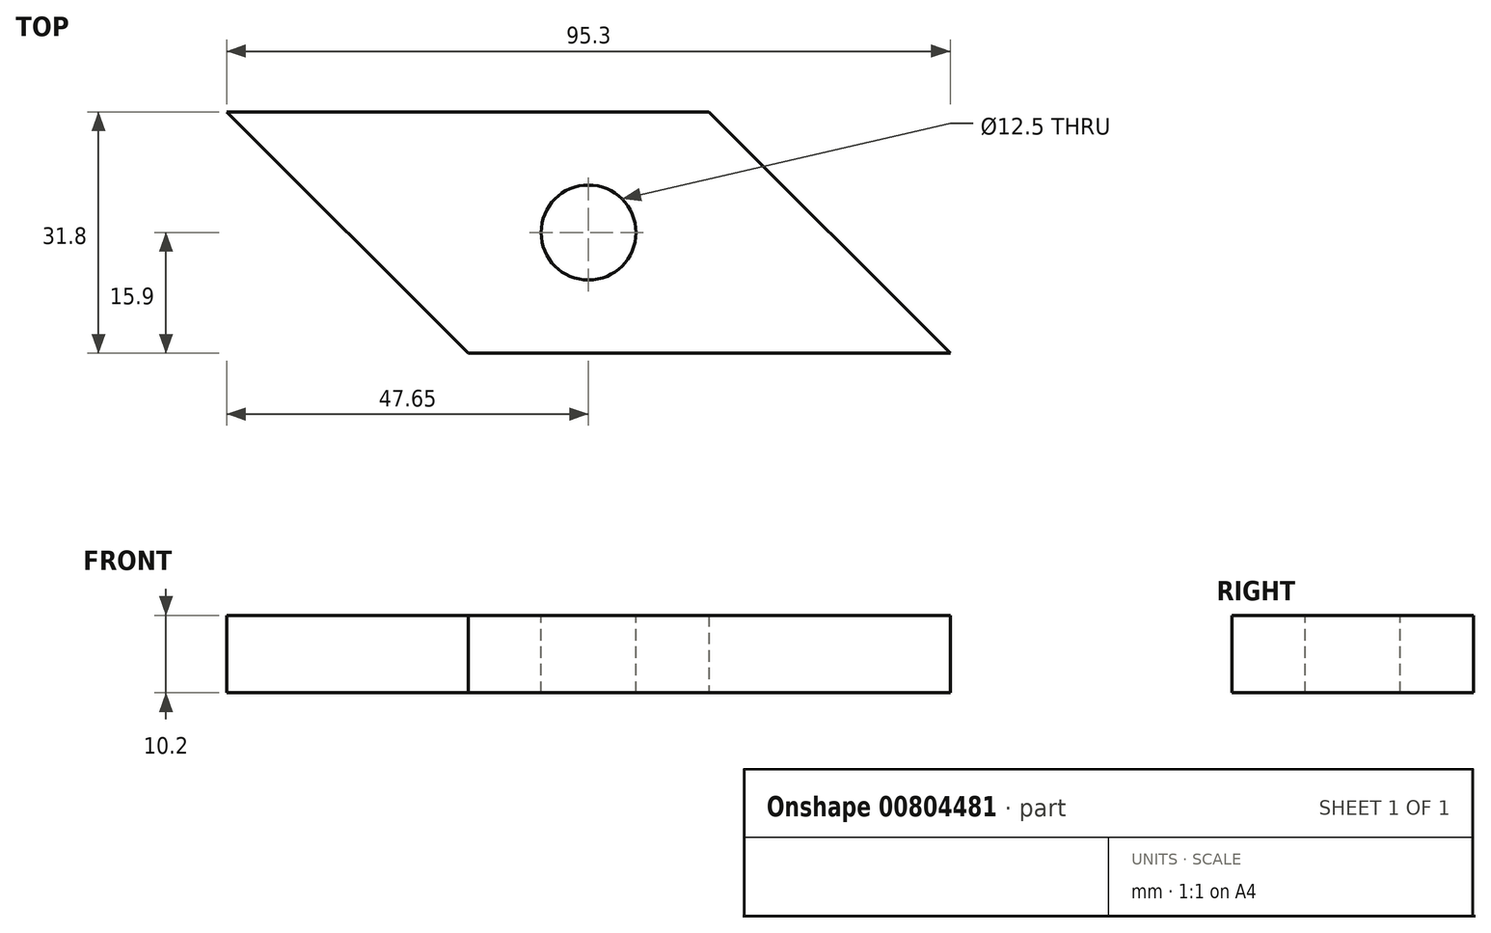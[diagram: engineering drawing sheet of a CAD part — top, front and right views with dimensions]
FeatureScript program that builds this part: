
annotation { "Feature Type Name" : "Feature", "Feature Type Description" : "" }
export const myFeature = defineFeature(function(context is Context, id is Id, definition is map)
    precondition{}
    {
        {
            var Q0;
            Q0=qCreatedBy(makeId("Top.planeOp"),FACE);
            var sketch = newSketch(context, id + "F0", { "sketchPlane" : qUnion([Q0])});
            skLineSegment(sketch, "E0", {"start": v(-47.65, 15.9) * mm, "end": v(15.85, 15.9) * mm});
            skLineSegment(sketch, "E1", {"start": v(15.85, 15.9) * mm, "end": v(47.65, -15.9) * mm});
            skLineSegment(sketch, "E2", {"start": v(47.65, -15.9) * mm, "end": v(-15.85, -15.9) * mm});
            skLineSegment(sketch, "E3", {"start": v(-47.65, 15.9) * mm, "end": v(-15.85, -15.9) * mm});
            skLineSegment(sketch, "E4", {"start": v(-15.85, -15.9) * mm, "end": v(15.85, 15.9) * mm, "construction": true});
            skSolve(sketch);
        }
        {
            var Q0;
            Q0=makeQuery(id+"F0.imprint","IMPRINT",FACE,{"disambiguationData":[TD([[makeQuery(id+"F0.imprint","IMPRINT",EDGE,{"derivedFrom":sQuery(id+"F0.wireOp",EDGE,"E0")}),-1.0]])]});
            var Q1;
            Q1=sQuery(id+"F0.wireOp",EDGE,"E4");
            var Q2;
            Q2=sQuery(id+"F0.wireOp",EDGE,"E0");
            var Q3;
            Q3=sQuery(id+"F0.wireOp",EDGE,"E3");
            var Q4;
            Q4=sQuery(id+"F0.wireOp",EDGE,"E2");
            var Q5;
            Q5=sQuery(id+"F0.wireOp",EDGE,"E1");
            extrude(context, id + "F1", {"entities" : qUnion([Q0]), "surfaceEntities" : qUnion([Q1, Q2, Q3, Q4, Q5]), "depth" : 10.2 * mm, "offsetDistance" : 25.4 * mm});
        }
        {
            var Q0;
            Q0=makeQuery(id+"F1.opExtrude","CAP_FACE",FACE,{"disambiguationData":[OSD([sQuery(id+"F0.wireOp",EDGE,"E0"),sQuery(id+"F0.wireOp",EDGE,"E1"),sQuery(id+"F0.wireOp",EDGE,"E2"),sQuery(id+"F0.wireOp",EDGE,"E3")])],"isStart":false});
            var sketch = newSketch(context, id + "F2", { "sketchPlane" : qUnion([Q0])});
            skCircle(sketch, "E5", {"center": v(0, 0) * mm, "radius": 6.25 * mm});
            skSolve(sketch);
        }
        {
            var Q0;
            Q0 = qSketchRegion(id + "F2", true);
            extrude(context, id + "F3", {"entities" : qUnion([Q0]), "operationType" : NewBodyOperationType.REMOVE, "endBound" : BoundingType.THROUGH_ALL, "oppositeDirection" : true, "depth" : 2 * mm, "offsetDistance" : 25.4 * mm});
        }
    });
